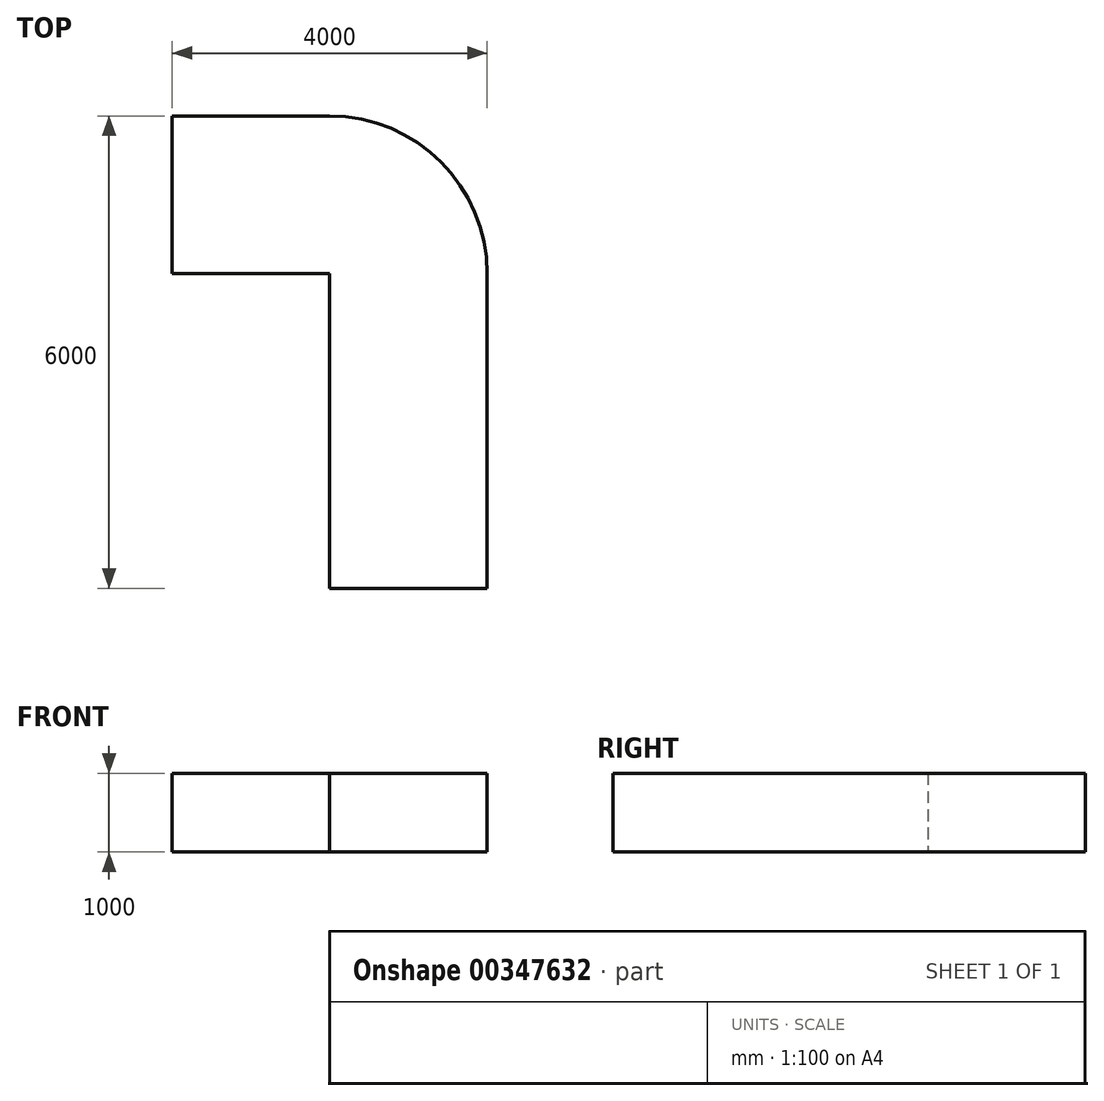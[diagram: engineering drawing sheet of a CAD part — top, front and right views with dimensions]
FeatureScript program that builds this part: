
annotation { "Feature Type Name" : "Feature", "Feature Type Description" : "" }
export const myFeature = defineFeature(function(context is Context, id is Id, definition is map)
    precondition{}
    {
        {
            var Q0;
            Q0=qCreatedBy(makeId("Top.planeOp"),FACE);
            var sketch = newSketch(context, id + "F0", { "sketchPlane" : qUnion([Q0])});
            skLineSegment(sketch, "E0.bottom", {"start": v(1000, 1000) * mm, "end": v(-1000, 1000) * mm});
            skLineSegment(sketch, "E0.top", {"start": v(1000, -1000) * mm, "end": v(-1000, -1000) * mm});
            skLineSegment(sketch, "E0.right", {"start": v(-1000, 1000) * mm, "end": v(-1000, -1000) * mm});
            skPoint(sketch, "E0.middle", {"position": v(0, 0) * mm});
            skArc(sketch, "E1", {"start": v(1000, 1000) * mm, "mid": v(2414.21, 414.21) * mm, "end": v(3000, -1000) * mm});
            skLineSegment(sketch, "E2.top", {"start": v(1000, -5000) * mm, "end": v(3000, -5000) * mm});
            skLineSegment(sketch, "E2.left", {"start": v(1000, -1000) * mm, "end": v(1000, -5000) * mm});
            skLineSegment(sketch, "E2.right", {"start": v(3000, -1000) * mm, "end": v(3000, -5000) * mm});
            skSolve(sketch);
        }
        {
            var Q0;
            Q0=makeQuery(id+"F0.imprint","IMPRINT",FACE,{"disambiguationData":[TD([[makeQuery(id+"F0.imprint","IMPRINT",EDGE,{"derivedFrom":sQuery(id+"F0.wireOp",EDGE,"E0.bottom")}),1.0]])]});
            extrude(context, id + "F1", {"entities" : qUnion([Q0]), "depth" : 1000 * mm});
        }
    });
